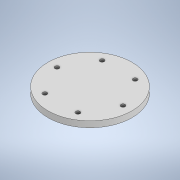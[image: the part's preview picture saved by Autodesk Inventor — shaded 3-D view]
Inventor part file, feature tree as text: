
AUTODESK INVENTOR PART (.ipt)
format: ipt  version: 2022.2 (Build 262287000, 287)  size: 391,680 bytes
history: native  units: in
note: dims shown in document units (in); Inventor stores cm internally (conversion verified against a paired STEP export)
features: sketch x2, extrude x1, hole x1, emboss x1
ambient origin geometry x8: Origin, YZ Plane, XZ Plane, XY Plane, X Axis, Y Axis, Z Axis, Center Point
bodies: Solid1 (feature_tree)
feature tree (5):
  extrude  "Extrusion1"  Depth=0.25in TaperAngle=0.0deg
  hole  "Hole1"  [1 undecoded]
  emboss  "Emboss1"
  sketch  "Sketch2"  dims[d0=3.5in d2=0.25in d3=0.0in]
  sketch  "Sketch4"  dims[d4=1.375in d5=2.3622in d7=360.0deg d9=0.177in d10=0.328in d11=0.332in d12=0.25in d13=0.5635in d14=1.0in d15=0.0in d19=2.0in d20=0.05in d21=0.0in]
note: 1 required parameter value undecoded (feature->parameter linkage not recoverable at this tier; creation-order binding heuristic only, values carry confidence <= 0.55)
